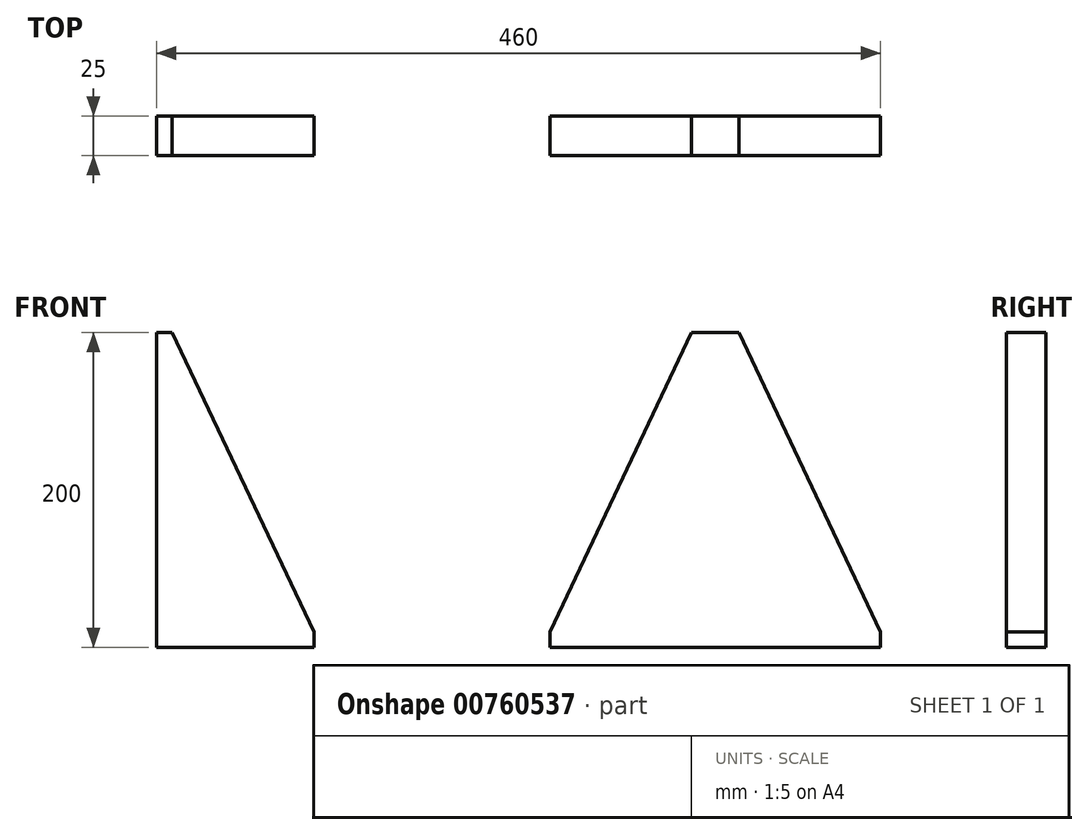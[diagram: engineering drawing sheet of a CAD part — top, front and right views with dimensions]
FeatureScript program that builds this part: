
annotation { "Feature Type Name" : "Feature", "Feature Type Description" : "" }
export const myFeature = defineFeature(function(context is Context, id is Id, definition is map)
    precondition{}
    {
        {
            var Q0;
            Q0=qCreatedBy(makeId("Front.planeOp"),FACE);
            var sketch = newSketch(context, id + "F0", { "sketchPlane" : qUnion([Q0])});
            skLineSegment(sketch, "E0", {"start": v(0, 0) * mm, "end": v(0, 10) * mm});
            skLineSegment(sketch, "E1", {"start": v(0, 10) * mm, "end": v(90, 200) * mm});
            skLineSegment(sketch, "E2", {"start": v(90, 200) * mm, "end": v(120, 200) * mm});
            skLineSegment(sketch, "E3", {"start": v(120, 200) * mm, "end": v(210, 10) * mm});
            skLineSegment(sketch, "E4", {"start": v(210, 10) * mm, "end": v(210, 0) * mm});
            skLineSegment(sketch, "E5", {"start": v(210, 0) * mm, "end": v(0, 0) * mm});
            skLineSegment(sketch, "E6", {"start": v(-250, 200) * mm, "end": v(-250, 0) * mm});
            skLineSegment(sketch, "E7", {"start": v(-250, 0) * mm, "end": v(-150, 0) * mm});
            skLineSegment(sketch, "E8", {"start": v(-150, 0) * mm, "end": v(-150, 10) * mm});
            skLineSegment(sketch, "E9", {"start": v(-150, 10) * mm, "end": v(-240, 200) * mm});
            skLineSegment(sketch, "E10", {"start": v(-250, 200) * mm, "end": v(-240, 200) * mm});
            skSolve(sketch);
        }
        {
            var Q0;
            Q0=makeQuery(id+"F0.imprint","IMPRINT",FACE,{"disambiguationData":[TD([[makeQuery(id+"F0.imprint","IMPRINT",EDGE,{"derivedFrom":sQuery(id+"F0.wireOp",EDGE,"E6")}),1.0]])]});
            extrude(context, id + "F1", {"entities" : qUnion([Q0]), "depth" : 25 * mm, "offsetDistance" : 25 * mm});
        }
        {
            var Q0;
            Q0=makeQuery(id+"F0.imprint","IMPRINT",FACE,{"disambiguationData":[TD([[makeQuery(id+"F0.imprint","IMPRINT",EDGE,{"derivedFrom":sQuery(id+"F0.wireOp",EDGE,"E0")}),-1.0]])]});
            extrude(context, id + "F2", {"entities" : qUnion([Q0]), "depth" : 25 * mm, "offsetDistance" : 25 * mm});
        }
    });
